# Revit family: Hager-Golf-IP40-Plain_Door-syst-NoHosted-CH-en
name_source: partatom
category: Electrical Equipment
units: mm (PartAtom-declared; Revit-internal decimal feet)

## family parameters
Always vertical = Yes
Cut with Voids When Loaded = No
Panel Configuration = Two Columns, Circuits Across
Part Type = Panelboard
Room Calculation Point = No
Round Connector Dimension = Use Diameter
Shared = No
Work Plane-Based = Yes

## types (22) — shared parameters
Default Elevation = 1219 mm
EF000007 - Colour = EV000202 - White
EF000116 - RAL-number = 9010
EF000118 - With mounting plate = No
EF000339 - Type of cover = EV004216 - Door
EF001062 - EMC-version = No
EF001088 - Extension possible = Yes
EF001596 - Material housing = EV000139 - Plastic
EF004462 - Type of closure = EV000154 - Other
EF006244 - Transparent cover/door = No
EF006306 - With lock = No
EF009212 - Cover model = EV000116 - Closed
EF015941 - Signal passing door = Yes
HG000001 - Number of columns = 1
HG000002 - With door or cover = Yes
HG000003 - Range = Golf
HG000005 - Thickness = 3 mm  [stored 0.00984252 ft]
HG000009 - Double swing door = No
HG000010 - Asymmetric doors = No
HG000011 - Empty rows from bottom = No
HG000017 - Distance between poles = 18 mm  [stored 0.0590551 ft]
Manufacturer = Hager
Type Comments = Golf
zero-valued in all types: HG000007 - Number of empty columns, HG000008 - Number of empty rows

## per-type parameters (varying)
| type | EF000003 - Mounting method | EF000008 - Width | EF000040 - Height | EF000049 - Depth | EF000218 - Built-in depth | EF000266 - Number of rows | EF000332 - Built-in height | EF000846 - Built-in width | EF001131 - Internal depth | EF001134 - DIN-rail | EF002950 - Width in number of modular spacings | EF005474 - Degree of protection (IP) | EF015776 - Earthing terminal block | EF015777 - Neutral terminal block | HG000004 - Manufacturer reference | HG000006 - Flush mounted | Model |
| Recessed mounted  W204 H225 D97.5 4 Modular spacings - VF104PS | EV000383 - Flush mounted (plaster) | 204 mm | 225 mm  [stored 0.738189 ft] | 98 mm  [stored 0.321522 ft] | 72 mm  [stored 0.23622 ft] | 1 | 189 mm  [stored 0.620079 ft] | 170 mm  [stored 0.557743 ft] | 98 mm  [stored 0.321522 ft] | Yes | 4 |  | No | No | VF104PS | Yes | VF104PS |
| Recessed mounted  W275 H225 D97.5 8 Modular spacings - VF108PS | EV000383 - Flush mounted (plaster) | 275 mm | 225 mm  [stored 0.738189 ft] | 98 mm  [stored 0.321522 ft] | 72 mm  [stored 0.23622 ft] | 1 | 189 mm  [stored 0.620079 ft] | 242 mm  [stored 0.793963 ft] | 98 mm  [stored 0.321522 ft] | Yes | 8 |  | No | No | VF108PS | Yes | VF108PS |
| Recessed mounted IP40 W352 H293 D97.5 12 Modular spacings - VF112PS | EV000383 - Flush mounted (plaster) | 352 mm  [stored 1.15486 ft] | 293 mm | 98 mm  [stored 0.321522 ft] | 72 mm  [stored 0.23622 ft] | 1 | 257 mm  [stored 0.843176 ft] | 318 mm  [stored 1.04331 ft] | 98 mm  [stored 0.321522 ft] | Yes | 12 | EV006415 - IP40 | Yes | Yes | VF112PS | Yes | VF112PS |
| Recessed mounted IP40 W352 H543 D97.5 12 Modular spacings - VF312PS | EV000383 - Flush mounted (plaster) | 352 mm  [stored 1.15486 ft] | 543 mm  [stored 1.7815 ft] | 98 mm  [stored 0.321522 ft] | 72 mm  [stored 0.23622 ft] | 3 | 507 mm  [stored 1.66339 ft] | 318 mm  [stored 1.04331 ft] | 98 mm  [stored 0.321522 ft] | Yes | 12 | EV006415 - IP40 | Yes | Yes | VF312PS | Yes | VF312PS |
| Recessed mounted IP40 W352 H688 D97.5 12 Modular spacings - VF412PS | EV000383 - Flush mounted (plaster) | 352 mm  [stored 1.15486 ft] | 688 mm  [stored 2.25722 ft] | 98 mm  [stored 0.321522 ft] | 72 mm  [stored 0.23622 ft] | 4 | 652 mm  [stored 2.13911 ft] | 318 mm  [stored 1.04331 ft] | 98 mm  [stored 0.321522 ft] | Yes | 12 | EV006415 - IP40 | Yes | Yes | VF412PS | Yes | VF412PS |
| Recessed mounted IP40 W382 H418 D97.5 12 Modular spacings - VF212PS | EV000383 - Flush mounted (plaster) | 382 mm  [stored 1.25328 ft] | 418 mm  [stored 1.37139 ft] | 98 mm  [stored 0.321522 ft] | 72 mm  [stored 0.23622 ft] | 2 | 382 mm  [stored 1.25328 ft] | 318 mm  [stored 1.04331 ft] | 98 mm  [stored 0.321522 ft] | Yes | 12 | EV006415 - IP40 | Yes | Yes | VF212PS | Yes | VF212PS |
| Recessed mounted IP40 W460 H293 D97.5 18 Modular spacings - VF118PS | EV000383 - Flush mounted (plaster) | 460 mm  [stored 1.50919 ft] | 293 mm | 98 mm  [stored 0.321522 ft] | 72 mm  [stored 0.23622 ft] | 1 | 257 mm  [stored 0.843176 ft] | 426 mm  [stored 1.39764 ft] | 98 mm  [stored 0.321522 ft] | Yes | 18 | EV006415 - IP40 | Yes | Yes | VF118PS | Yes | VF118PS |
| Recessed mounted IP40 W460 H418 D97.5 18 Modular spacings - VF218PS | EV000383 - Flush mounted (plaster) | 460 mm  [stored 1.50919 ft] | 418 mm  [stored 1.37139 ft] | 98 mm  [stored 0.321522 ft] | 72 mm  [stored 0.23622 ft] | 2 | 382 mm  [stored 1.25328 ft] | 426 mm  [stored 1.39764 ft] | 98 mm  [stored 0.321522 ft] | Yes | 18 | EV006415 - IP40 | Yes | Yes | VF218PS | Yes | VF218PS |
| Recessed mounted IP40 W460 H543 D97.5 18 Modular spacings - VF318PS | EV000383 - Flush mounted (plaster) | 460 mm  [stored 1.50919 ft] | 543 mm  [stored 1.7815 ft] | 98 mm  [stored 0.321522 ft] | 72 mm  [stored 0.23622 ft] | 3 | 507 mm  [stored 1.66339 ft] | 426 mm  [stored 1.39764 ft] | 98 mm  [stored 0.321522 ft] | Yes | 18 | EV006415 - IP40 | Yes | Yes | VF318PS | Yes | VF318PS |
| Recessed mounted IP40 W460 H688 D97.5 18 Modular spacings - VF418PS | EV000383 - Flush mounted (plaster) | 460 mm  [stored 1.50919 ft] | 688 mm  [stored 2.25722 ft] | 98 mm  [stored 0.321522 ft] | 72 mm  [stored 0.23622 ft] | 4 | 652 mm  [stored 2.13911 ft] | 426 mm  [stored 1.39764 ft] | 98 mm  [stored 0.321522 ft] | Yes | 18 | EV006415 - IP40 | Yes | Yes | VF418PS | Yes | VF418PS |
| Recessed mounted IP40 W532 H293 D97.5 22 Modular spacings - VF122PS | EV000383 - Flush mounted (plaster) | 532 mm  [stored 1.74541 ft] | 293 mm | 98 mm  [stored 0.321522 ft] | 72 mm  [stored 0.23622 ft] | 1 | 257 mm  [stored 0.843176 ft] | 498 mm  [stored 1.63386 ft] | 98 mm  [stored 0.321522 ft] | Yes | 22 | EV006415 - IP40 | Yes | Yes | VF122PS | Yes | VF122PS |
| Surface mounted  W138 H184 D99 4 Modular spacings - VS104PS | EV000384 - Surface mounted (plaster) | 138 mm  [stored 0.452756 ft] | 184 mm  [stored 0.603675 ft] | 99 mm  [stored 0.324803 ft] | 0 mm  [stored 0 ft] | 1 | 0 mm  [stored 0 ft] | 0 mm  [stored 0 ft] | 99 mm  [stored 0.324803 ft] | Yes | 4 |  | No | No | VS104PS | No | VS104PS |
| Surface mounted  W210 H184 D99 8 Modular spacings - VS108PS | EV000384 - Surface mounted (plaster) | 210 mm  [stored 0.688976 ft] | 184 mm  [stored 0.603675 ft] | 99 mm  [stored 0.324803 ft] | 0 mm  [stored 0 ft] | 1 | 0 mm  [stored 0 ft] | 0 mm  [stored 0 ft] | 99 mm  [stored 0.324803 ft] | No | 8 |  | No | No | VS108PS | No | VS108PS |
| Surface mounted IP40 W282 H252 D99 12 Modular spacings - VS112PS | EV000384 - Surface mounted (plaster) | 282 mm | 252 mm  [stored 0.826772 ft] | 99 mm  [stored 0.324803 ft] | 0 mm  [stored 0 ft] | 1 | 0 mm  [stored 0 ft] | 0 mm  [stored 0 ft] | 99 mm  [stored 0.324803 ft] | Yes | 12 | EV006415 - IP40 | Yes | Yes | VS112PS | No | VS112PS |
| Surface mounted IP40 W282 H377 D99 12 Modular spacings - VS212PS | EV000384 - Surface mounted (plaster) | 282 mm | 377 mm  [stored 1.23688 ft] | 99 mm  [stored 0.324803 ft] | 0 mm  [stored 0 ft] | 2 | 0 mm  [stored 0 ft] | 0 mm  [stored 0 ft] | 99 mm  [stored 0.324803 ft] | Yes | 12 | EV006415 - IP40 | Yes | Yes | VS212PS | No | VS212PS |
| Surface mounted IP40 W282 H500 D99 12 Modular spacings - VS312PS | EV000384 - Surface mounted (plaster) | 282 mm | 500 mm  [stored 1.64042 ft] | 99 mm  [stored 0.324803 ft] | 0 mm  [stored 0 ft] | 3 | 0 mm  [stored 0 ft] | 0 mm  [stored 0 ft] | 99 mm  [stored 0.324803 ft] | Yes | 12 | EV006415 - IP40 | Yes | Yes | VS312PS | No | VS312PS |
| Surface mounted IP40 W282 H647 D99 12 Modular spacings - VS412PS | EV000384 - Surface mounted (plaster) | 282 mm | 647 mm  [stored 2.1227 ft] | 99 mm  [stored 0.324803 ft] | 0 mm  [stored 0 ft] | 4 | 0 mm  [stored 0 ft] | 0 mm  [stored 0 ft] | 99 mm  [stored 0.324803 ft] | Yes | 12 | EV006415 - IP40 | Yes | Yes | VS412PS | No | VS412PS |
| Surface mounted IP40 W390 H252 D99 18 Modular spacings - VS118PS | EV000384 - Surface mounted (plaster) | 390 mm  [stored 1.27953 ft] | 252 mm  [stored 0.826772 ft] | 99 mm  [stored 0.324803 ft] | 0 mm  [stored 0 ft] | 1 | 0 mm  [stored 0 ft] | 0 mm  [stored 0 ft] | 99 mm  [stored 0.324803 ft] | Yes | 18 | EV006415 - IP40 | Yes | Yes | VS118PS | No | VS118PS |
| Surface mounted IP40 W390 H377 D99 18 Modular spacings - VS218PS | EV000384 - Surface mounted (plaster) | 390 mm  [stored 1.27953 ft] | 377 mm  [stored 1.23688 ft] | 99 mm  [stored 0.324803 ft] | 0 mm  [stored 0 ft] | 2 | 0 mm  [stored 0 ft] | 0 mm  [stored 0 ft] | 99 mm  [stored 0.324803 ft] | Yes | 18 | EV006415 - IP40 | Yes | Yes | VS218PS | No | VS218PS |
| Surface mounted IP40 W390 H500 D99 18 Modular spacings - VS318PS | EV000384 - Surface mounted (plaster) | 390 mm  [stored 1.27953 ft] | 500 mm  [stored 1.64042 ft] | 99 mm  [stored 0.324803 ft] | 0 mm  [stored 0 ft] | 3 | 0 mm  [stored 0 ft] | 0 mm  [stored 0 ft] | 99 mm  [stored 0.324803 ft] | Yes | 18 | EV006415 - IP40 | Yes | Yes | VS318PS | No | VS318PS |
| Surface mounted IP40 W390 H647 D99 18 Modular spacings - VS418PS | EV000384 - Surface mounted (plaster) | 390 mm  [stored 1.27953 ft] | 647 mm  [stored 2.1227 ft] | 99 mm  [stored 0.324803 ft] | 0 mm  [stored 0 ft] | 4 | 0 mm  [stored 0 ft] | 0 mm  [stored 0 ft] | 99 mm  [stored 0.324803 ft] | Yes | 18 | EV006415 - IP40 | Yes | Yes | VS418PS | No | VS418PS |
| Surface mounted IP40 W462 H252 D99 22 Modular spacings - VS122PS | EV000384 - Surface mounted (plaster) | 462 mm  [stored 1.51575 ft] | 252 mm  [stored 0.826772 ft] | 99 mm  [stored 0.324803 ft] | 0 mm  [stored 0 ft] | 1 | 0 mm  [stored 0 ft] | 0 mm  [stored 0 ft] | 99 mm  [stored 0.324803 ft] | Yes | 22 | EV006415 - IP40 | Yes | Yes | VS122PS | No | VS122PS |

note: [stored X ft] marks values corroborated as IEEE doubles in the binary element streams (Revit-internal decimal feet)

## geometry (parser evidence)
native form markers: Sweep x14
no freeform markers — native parametric forms only
